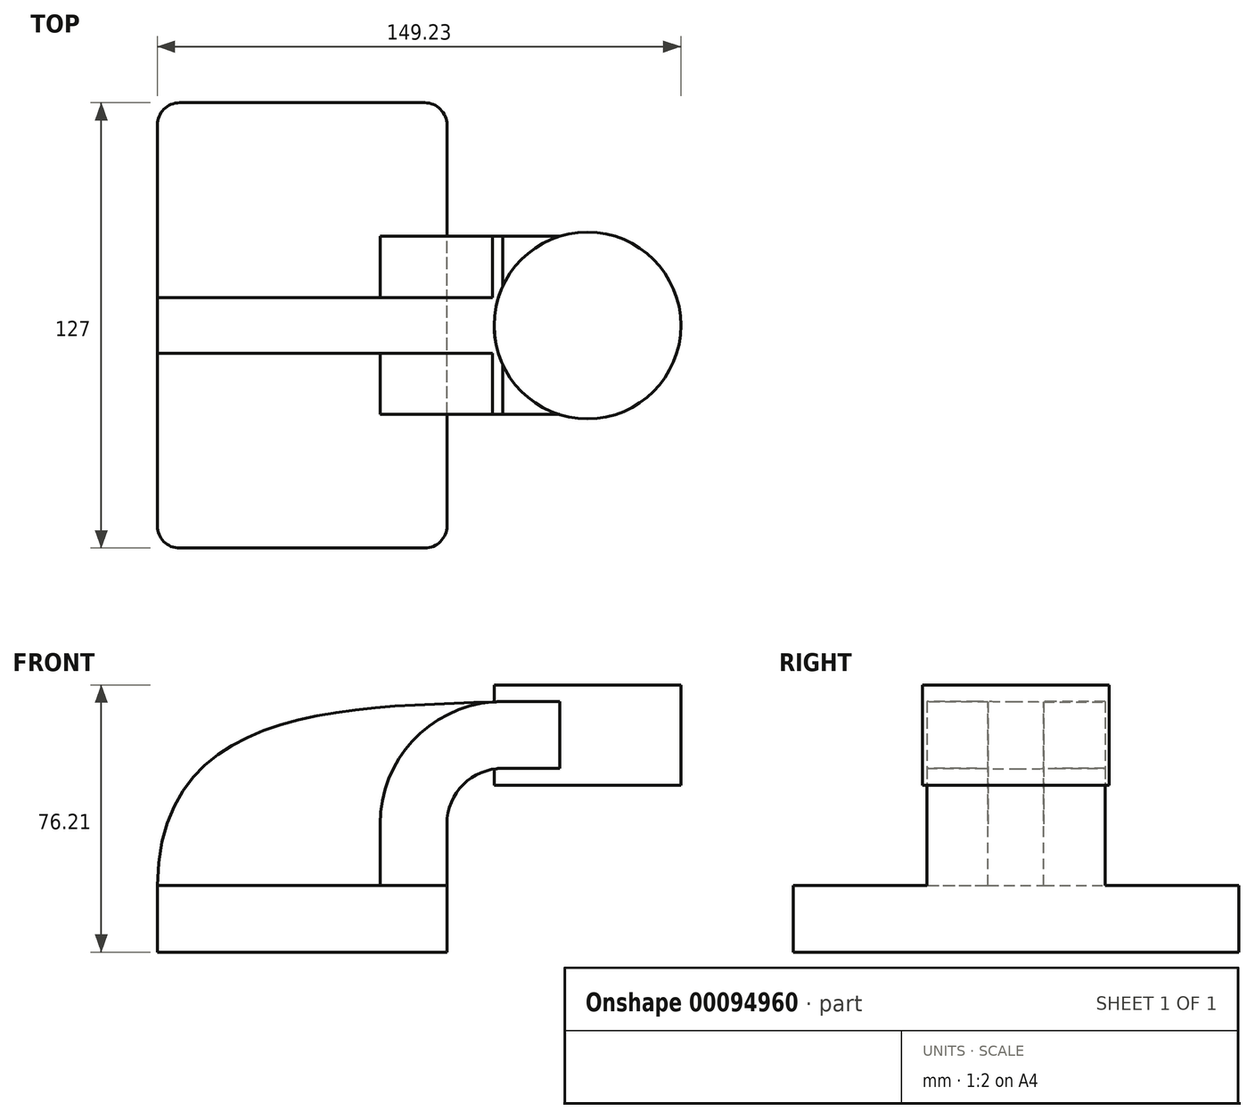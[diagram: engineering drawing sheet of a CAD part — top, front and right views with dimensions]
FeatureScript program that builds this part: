
annotation { "Feature Type Name" : "Feature", "Feature Type Description" : "" }
export const myFeature = defineFeature(function(context is Context, id is Id, definition is map)
    precondition{}
    {
        {
            var Q0;
            Q0=qCreatedBy(makeId("Front.planeOp"),FACE);
            var sketch = newSketch(context, id + "F0", { "sketchPlane" : qUnion([Q0])});
            skLineSegment(sketch, "E0.bottom", {"start": v(-41.28, 9.52) * mm, "end": v(41.27, 9.53) * mm});
            skLineSegment(sketch, "E0.top", {"start": v(-41.28, -9.53) * mm, "end": v(41.28, -9.53) * mm});
            skLineSegment(sketch, "E0.left", {"start": v(-41.28, 9.52) * mm, "end": v(-41.27, -9.53) * mm});
            skLineSegment(sketch, "E0.right", {"start": v(41.28, 9.53) * mm, "end": v(41.28, -9.52) * mm});
            skPoint(sketch, "E0.middle", {"position": v(0, 0) * mm});
            skLineSegment(sketch, "E1.bottom", {"start": v(107.95, 38.1) * mm, "end": v(57.15, 38.1) * mm});
            skLineSegment(sketch, "E1.top", {"start": v(107.95, 66.67) * mm, "end": v(57.15, 66.67) * mm});
            skLineSegment(sketch, "E1.left", {"start": v(107.95, 38.1) * mm, "end": v(107.95, 66.67) * mm});
            skLineSegment(sketch, "E1.right", {"start": v(57.15, 38.1) * mm, "end": v(57.15, 66.67) * mm});
            skPoint(sketch, "E1.middle", {"position": v(82.55, 52.39) * mm});
            skLineSegment(sketch, "E2", {"start": v(41.27, 9.53) * mm, "end": v(41.27, 27) * mm});
            skArc(sketch, "E3", {"start": v(41.27, 27) * mm, "mid": v(45.92, 38.23) * mm, "end": v(57.15, 42.88) * mm});
            skLineSegment(sketch, "E4", {"start": v(57.15, 42.88) * mm, "end": v(81.34, 42.88) * mm});
            skLineSegment(sketch, "E5.0", {"start": v(57.15, 61.93) * mm, "end": v(81.34, 61.93) * mm});
            skArc(sketch, "E5.1", {"start": v(22.22, 27) * mm, "mid": v(32.45, 51.7) * mm, "end": v(57.15, 61.93) * mm});
            skLineSegment(sketch, "E5.2", {"start": v(22.22, 9.53) * mm, "end": v(22.22, 27) * mm});
            skLineSegment(sketch, "E6", {"start": v(81.34, 38.1) * mm, "end": v(81.34, 66.67) * mm});
            skFitSpline(sketch, "E7", {"points": [v(-41.28, 9.52) * mm, v(57.15, 61.93) * mm], "startDerivative": vector(1.9, 159.3) * mm, "endDerivative": vector(123.34, 5.36) * mm});
            skSolve(sketch);
        }
        {
            var Q0;
            Q0=makeQuery(id+"F0.imprint","IMPRINT",FACE,{"disambiguationData":[TD([[makeQuery(id+"F0.imprint","IMPRINT",EDGE,{"derivedFrom":sQuery(id+"F0.wireOp",EDGE,"E0.top")}),1.0]])]});
            extrude(context, id + "F1", {"entities" : qUnion([Q0]), "endBound" : BoundingType.SYMMETRIC, "depth" : 127 * mm});
        }
        {
            var Q0;
            {var subQ1=sQuery(id+"F0.wireOp",EDGE,"E2");Q0=makeQuery(id+"F0.imprint","IMPRINT",FACE,{"disambiguationData":[TD([[makeQuery(id+"F0.imprint","IMPRINT",EDGE,{"derivedFrom":subQ1}),1.0]])]});}
            var Q1;
            {var subQ0=sQuery(id+"F0.wireOp",EDGE,"E4");Q1=makeQuery(id+"F0.imprint","IMPRINT",FACE,{"disambiguationData":[TD([[makeQuery(id+"F0.imprint","IMPRINT",EDGE,{"derivedFrom":subQ0}),1.0]])]});}
            extrude(context, id + "F2", {"entities" : qUnion([Q0, Q1]), "operationType" : NewBodyOperationType.ADD, "endBound" : BoundingType.SYMMETRIC, "depth" : 50.8 * mm});
        }
        {
            var Q0;
            {var subQ3=sQuery(id+"F0.wireOp",EDGE,"E5.2");Q0=makeQuery(id+"F0.imprint","IMPRINT",FACE,{"disambiguationData":[TD([[makeQuery(id+"F0.imprint","IMPRINT",EDGE,{"derivedFrom":subQ3}),1.0]])]});}
            extrude(context, id + "F3", {"entities" : qUnion([Q0]), "operationType" : NewBodyOperationType.ADD, "endBound" : BoundingType.SYMMETRIC, "depth" : 15.88 * mm});
        }
        {
            var Q0;
            {var subQ0=sQuery(id+"F0.wireOp",EDGE,"E1.left");Q0=makeQuery(id+"F0.imprint","IMPRINT",FACE,{"disambiguationData":[TD([[makeQuery(id+"F0.imprint","IMPRINT",EDGE,{"derivedFrom":subQ0}),1.0]])]});}
            var Q1;
            Q1=sQuery(id+"F0.wireOp",EDGE,"E6");
            revolve(context, id + "F4", {"operationType" : NewBodyOperationType.ADD, "entities" : qUnion([Q0]), "axis" : qUnion([Q1]), "revolveType" : RevolveType.FULL});
        }
        {
            var Q0;
            Q0=makeQuery(id+"F1.opExtrude","CAP_EDGE",EDGE,{"disambiguationData":[OSD([sQuery(id+"F0.wireOp",EDGE,"E0.right")])],"isStart":false});
            var Q1;
            Q1=makeQuery(id+"F1.opExtrude","CAP_EDGE",EDGE,{"disambiguationData":[OSD([sQuery(id+"F0.wireOp",EDGE,"E0.left")])],"isStart":false});
            var Q2;
            Q2=makeQuery(id+"F1.opExtrude","CAP_EDGE",EDGE,{"disambiguationData":[OSD([sQuery(id+"F0.wireOp",EDGE,"E0.right")])],"isStart":true});
            var Q3;
            Q3=makeQuery(id+"F1.opExtrude","CAP_EDGE",EDGE,{"disambiguationData":[OSD([sQuery(id+"F0.wireOp",EDGE,"E0.left")])],"isStart":true});
            fillet(context, id + "F5", {"entities" : qUnion([Q0, Q1, Q2, Q3]), "radius" : 6.35 * mm, "tangentPropagation" : true, "allowEdgeOverflow" : false});
        }
    });
